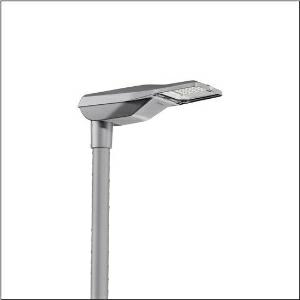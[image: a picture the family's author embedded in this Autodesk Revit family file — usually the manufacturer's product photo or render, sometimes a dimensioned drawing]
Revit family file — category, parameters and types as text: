
# Revit family: streetlight_sl_21_iq_micro___st1_0a_5xe1d41g08db_b7c0
name_source: partatom
category: Lighting Fixtures
units: mm (PartAtom-declared; Revit-internal decimal feet)

## family parameters
Cut with Voids When Loaded = No
Host = Face
Light Source = No
Part Type = Normal
Room Calculation Point = No
Round Connector Dimension = Use Diameter
Shared = No

## types (1)
- --- (1 x LED, 5010 lm, 36.4 W, 4000K)
    Apparent Load = 36 VA
    CIE Flux Codes = 37 72 97 100 100
    Color Rendering = 70
    Color Temperature = 4000K
    Default Elevation = 1800 mm
    Description = Streetlight SL 21 iQ micro, mast luminaire, primary light control with lens, of PMMA, primary optical cover: cover, of toughened safety glass, transparent, light distribution: ST1.0a, light emission: direct distribution, primary light characteristic: asymmetric, installation type: post-top, side-entry, LED, High Power LED, rated luminous flux: 5.010lm, luminous efficacy: 138lm/W, light colour: 740, colour temperature: 4000K, control gear: iQ Street-Remote, control: Street-Remote, Auto-Match, Temp-Guard, Lumen-Switch, Night-Set, Smart-Wire, Light-Fading, Desk-Remote (wireless, voltage-free reading and setting of iQ features in the workshop via application-optimized NFC function/RFID function), optimised constant luminous flux control (CLO 2.0), pre-setting: linear dimming characteristic, mains connection: 220..240V, AC, 50/60Hz, start of lifetime: 36W, end of service life: 38W, reduction: 16W, luminaire housing, of diecast aluminium, powder-coated, SITECO metallic grey (DB 702S), corrosivity category C5 high according to DIN EN ISO 12944, please order mast flange separately, inclination adjustable: 0°, 5°, 10°, 15°, sealing non-destructively replaceable, multi-level sealing system, length: 528mm, width: 235mm, height: 110mm, mast flange for spigot size: 42mm (side-entry): 5XC10008XM4, 60/48mm (side-entry/post-top): 5XC10108XM2, 76/60mm (side-entry/post-top): 5XC10108XM1, protection rating (complete): IP66, insulation class (complete): insulation class II (safety insulation), certification: CE, ENEC, ENEC+, VDE, impact resistance: IK10, permissible operating ambient temperature for outdoor applications: -40..+50°C, standard-compliant lighting for roads and squares, packaging unit: 1 piece

Light Distribution: ST1.0a
    Height = 110 mm
    Lamp = 1 x LED
    Lamp Light Flux = 5010 lm
    Lamp Power = 36.4 W
    Lamp count = 1
    Length = 528 mm
    Luminous efficacy = 138 lm/W
    Manufacturer = Siteco
    ModVariant = No
    Model = 5XE1D41G08DB
    Number of Poles = 1
    OnlyDefault = Yes
    Power Factor = 1
    Product Name = Streetlight SL 21 iQ micro | ST1.0a
    Product group = mast luminaire | pylon top
    ProductGroupID = 6100
    Protection Class = Protection class II
    Protection Degree = IP 66
    RLX_Detail_Level = 1
    RLX_Emergency_Light_Flux = 0 lm
    RLX_Emergency_Type = 0
    RLX_Emergency_Type_DB = No
    RlxData = <blob elided: 98917 chars, md5=01b8060d>
    Socket = socket
    Standby Power = 0 W
    System Light Flux = 5010 lm
    System Power = 36 W
    Type Comments = factory setting: luminous flux: 100 % | dim-lin: 254 | 715 mA
    Type Image = l_1006881.jpg
    URL = http://relux.com
    VarID = @adj_155403
    Voltage = 0 V
    Weight = 0.00 kg
    Width = 235 mm

## geometry (parser evidence)
native form markers: Blend x4, Sweep x9
no freeform markers — native parametric forms only
